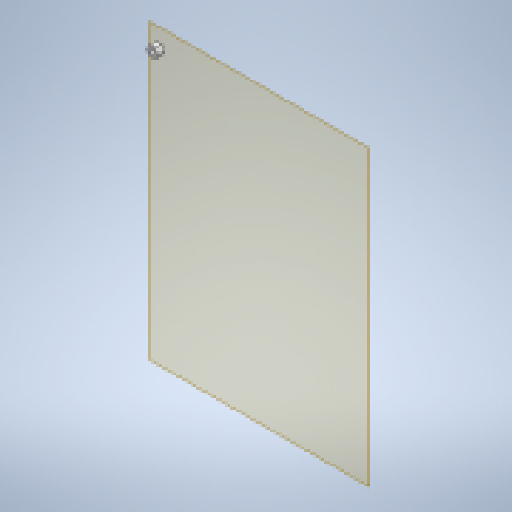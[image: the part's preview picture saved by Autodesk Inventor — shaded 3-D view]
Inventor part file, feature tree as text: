
AUTODESK INVENTOR PART (.ipt)
format: ipt  version: 2023 (Build 270158030, 158C)  size: 145,920 bytes
history: native  units: mm
features: other x3, plane x1, extrude x1, sketch x1
ambient origin geometry x8: Origin, YZ Plane, XZ Plane, XY Plane, X Axis, Y Axis, Z Axis, Center Point
bodies: Solid1 (feature_tree)
feature tree (6):
  plane  "Work Plane1"
  extrude  "Extrusion1"  Depth=11.85mm
  sketch  "Sketch1"  dims[d0=17.0mm d1=7.4mm d2=11.85mm d3=0.0mm]
  other  "<userpath>\Documents\0004-inventor\Inventor_Projects\electronics-enclosure\enclosure.iam"
  other  "enclosure.iam"
  other  "assembly-board:1"
